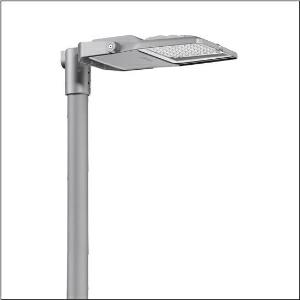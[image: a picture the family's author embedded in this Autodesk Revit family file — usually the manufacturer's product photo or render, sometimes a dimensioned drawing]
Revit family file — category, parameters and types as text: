
# Revit family: floodlight_fl_21_iq_mini___pl61_5xa7771c2c3a_2691
name_source: partatom
category: Lighting Fixtures
units: mm (PartAtom-declared; Revit-internal decimal feet)

## family parameters
Cut with Voids When Loaded = No
Host = Face
Light Source = No
Part Type = Normal
Room Calculation Point = No
Round Connector Dimension = Use Diameter
Shared = No

## types (1)
- --- (1 x LED, 11980 lm, 87.2 W, 3000K)
    Apparent Load = 87 VA
    CIE Flux Codes = 33 65 98 100 100
    Color Rendering = 70
    Color Temperature = 3000K
    Default Elevation = 1800 mm
    Description = Floodlight FL 21 iQ mini, floodlight, primary light control with lens, of PMMA, primary optical cover: protective disc, of toughened safety glass, transparent, light distribution: PL61, light emission: direct distribution, installation type: surface-mounted, LED, High Power LED, rated luminous flux: 11.980lm, luminous efficacy: 137lm/W, light colour: 730, colour temperature: 3000K, control: Auto-Match, Temp-Guard, Lumen-Switch, Night-Set, Smart-Wire, Light-Fading, Desk-Remote (wireless, voltage-free reading and setting of iQ features in the workshop via application-optimized NFC function/RFID function), optimised constant luminous flux control (CLO 2.0), with terminal, 6-pole, mains connection: 220..240V, AC, 50/60Hz, start of lifetime: 87W, end of service life: 92W, reduction: 40W, luminaire housing, of diecast aluminium, powder-coated, Siteco® metallic grey (DB 702S), corrosivity category C5 mid according to DIN EN ISO 12944, sealing non-destructively replaceable, please order mast flange separately, mast bracket, of steel, galvanised, powder-coated, Siteco® metallic grey (DB 702S), protection rating (complete): IP66, insulation class (complete): insulation class II (safety insulation), certification: CE, ENEC, VDE, protection symbol: D, impact resistance: IK08, permissible operating ambient temperature: -40..+40°C, permissible operating ambient temperature for outdoor applications: -40..+50°C, standard: DIN EN 12944, LABS conformity tested according to VDMA 24364:2018-05, packaging unit: 1 piece

Light Distribution: PL61
    Height = 70 mm
    Lamp = 1 x LED
    Lamp Light Flux = 11980 lm
    Lamp Power = 87.2 W
    Lamp count = 1
    Length = 485 mm
    Luminous efficacy = 137 lm/W
    Manufacturer = Siteco
    ModVariant = No
    Model = 5XA7771C2C3A
    Number of Poles = 1
    OnlyDefault = Yes
    Power Factor = 1
    Product Name = Floodlight FL 21 iQ mini | PL61
    Product group = floodlight | pylon annexe
    ProductGroupID = 6200
    Protection Class = Protection class II
    Protection Degree = IP 66
    RLX_Detail_Level = 1
    RLX_Emergency_Light_Flux = 0 lm
    RLX_Emergency_Type = 0
    RLX_Emergency_Type_DB = No
    RlxData = <blob elided: 101477 chars, md5=996d452d>
    Socket = socket
    Standby Power = 0 W
    System Light Flux = 11980 lm
    System Power = 87 W
    Type Comments = factory setting: luminous flux: 100 % | dim-lin: 254 | 456 mA
    Type Image = l_1007125.jpg
    URL = http://relux.com
    VarID = @adj_124223
    Voltage = 0 V
    Weight = 0.00 kg
    Width = 337 mm

## geometry (parser evidence)
native form markers: Blend x4, Sweep x11
no freeform markers — native parametric forms only
